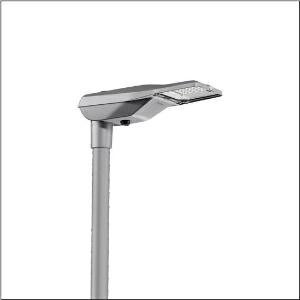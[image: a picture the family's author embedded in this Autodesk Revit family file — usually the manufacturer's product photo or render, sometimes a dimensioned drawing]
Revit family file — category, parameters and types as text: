
# Revit family: streetlight_sl_21_micro___st1_0ab_5xe1m33r08db_c8c0
name_source: partatom
category: Lighting Fixtures
units: mm (PartAtom-declared; Revit-internal decimal feet)

## family parameters
Cut with Voids When Loaded = No
Host = Face
Light Source = No
Part Type = Normal
Room Calculation Point = No
Round Connector Dimension = Use Diameter
Shared = No

## types (1)
- --- (1 x LED, 4500 lm, 39.1 W, 3000K)
    Apparent Load = 39 VA
    CIE Flux Codes = 38 73 97 100 100
    Color Rendering = 70
    Color Temperature = 3000K
    Default Elevation = 1800 mm
    Description = Streetlight SL 21 micro, mast luminaire, primary light control with lens, of PMMA, primary optical cover: cover, of toughened safety glass, transparent, light distribution: ST1.0aB, light emission: direct distribution, primary light characteristic: asymmetric, installation type: side-entry, post-top, LED, High Power LED, rated luminous flux: 4.500lm, luminous efficacy: 115lm/W, light colour: 730, colour temperature: 3000K, control: flexible luminous flux parameterisation, time-dependent luminous flux control, constant luminous flux control, overheat protection, presetting dimming logarithmic, mains connection: 220..240V, AC, 50/60Hz, start of lifetime: 39W, end of service life: 41W, reduction: 18W, luminaire housing, of diecast aluminium, powder-coated, Siteco® metallic grey (DB 702S), corrosivity category C5 mid according to DIN EN ISO 12944, please order mast flange separately, inclination adjustable: 0°, 5°, 10°, 15°, sealing non-destructively replaceable, multi-level sealing system, length: 528mm, width: 235mm, height: 110mm, mast flange for spigot size: 42mm (side-entry): 5XC10008XM4, 60/48mm (side-entry/post-top): 5XC10108XM2, 76/60mm (side-entry/post-top): 5XC10108XM1, Smart Interface below, protection rating (complete): IP66, insulation class (complete): insulation class II (safety insulation), certification: CE, ENEC, ENEC+, VDE, impact resistance: IK09, permissible operating ambient temperature for outdoor applications: -40..+50°C, standard-compliant lighting for roads and squares, packaging unit: 1 piece

Light Distribution: ST1.0aB
    Height = 110 mm
    Lamp = 1 x LED
    Lamp Light Flux = 4500 lm
    Lamp Power = 39.1 W
    Lamp count = 1
    Length = 528 mm
    Luminous efficacy = 115 lm/W
    Manufacturer = Siteco
    ModVariant = No
    Model = 5XE1M33R08DB
    Number of Poles = 1
    OnlyDefault = Yes
    Power Factor = 1
    Product Name = Streetlight SL 21 micro | ST1.0aB
    Product group = mast luminaire | pylon top
    ProductGroupID = 6100
    Protection Class = Protection class II
    Protection Degree = IP 66
    RLX_Detail_Level = 1
    RLX_Emergency_Light_Flux = 0 lm
    RLX_Emergency_Type = 0
    RLX_Emergency_Type_DB = No
    RlxData = <blob elided: 99093 chars, md5=c9301d8f>
    Socket = socket
    Standby Power = 0 W
    System Light Flux = 4500 lm
    System Power = 39 W
    Type Comments = factory setting: luminous flux: 100 % | dim-lin: 254 | 765 mA
    Type Image = l_1277290.jpg
    URL = http://relux.com
    VarID = @adj_104171
    Voltage = 0 V
    Weight = 0.00 kg
    Width = 235 mm

## geometry (parser evidence)
native form markers: Blend x4, Sweep x10
no freeform markers — native parametric forms only
